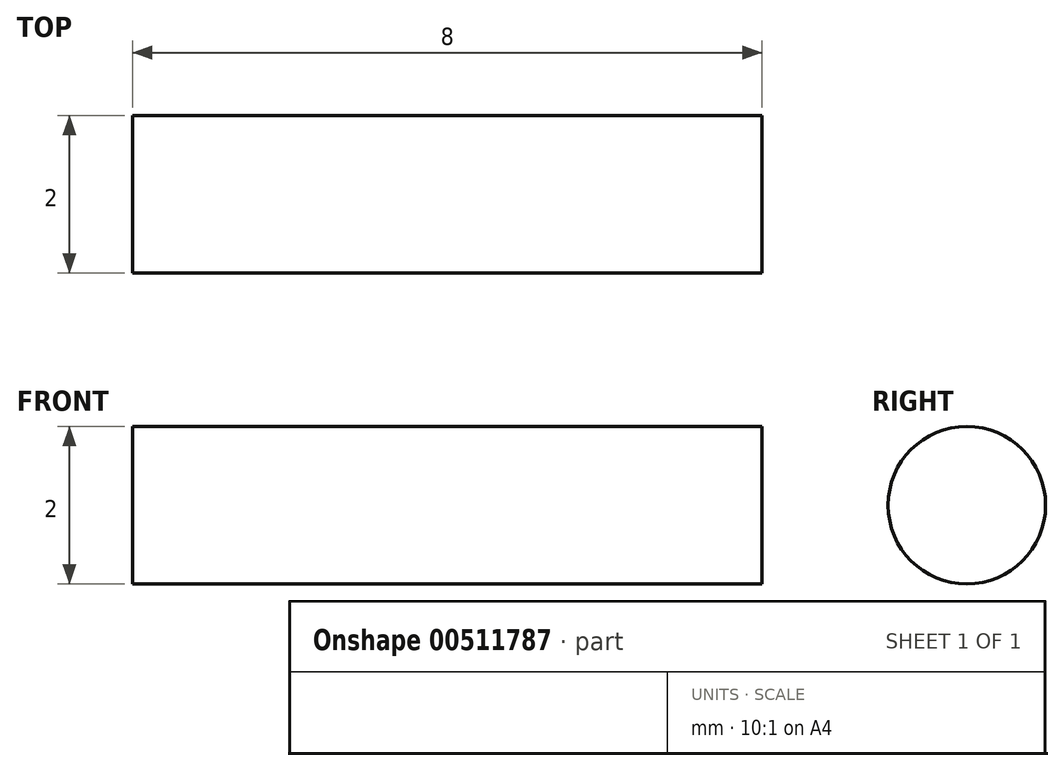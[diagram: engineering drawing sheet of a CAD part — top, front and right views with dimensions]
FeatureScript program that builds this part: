
annotation { "Feature Type Name" : "Feature", "Feature Type Description" : "" }
export const myFeature = defineFeature(function(context is Context, id is Id, definition is map)
    precondition{}
    {
        {
            var Q0;
            Q0=qCreatedBy(makeId("Right.planeOp"),FACE);
            var sketch = newSketch(context, id + "F0", { "sketchPlane" : qUnion([Q0])});
            skCircle(sketch, "E0", {"center": v(0, 0) * mm, "radius": 1 * mm});
            skSolve(sketch);
        }
        {
            var Q0;
            Q0 = qSketchRegion(id + "F0", true);
            extrude(context, id + "F1", {"entities" : qUnion([Q0]), "depth" : 8 * mm});
        }
    });
